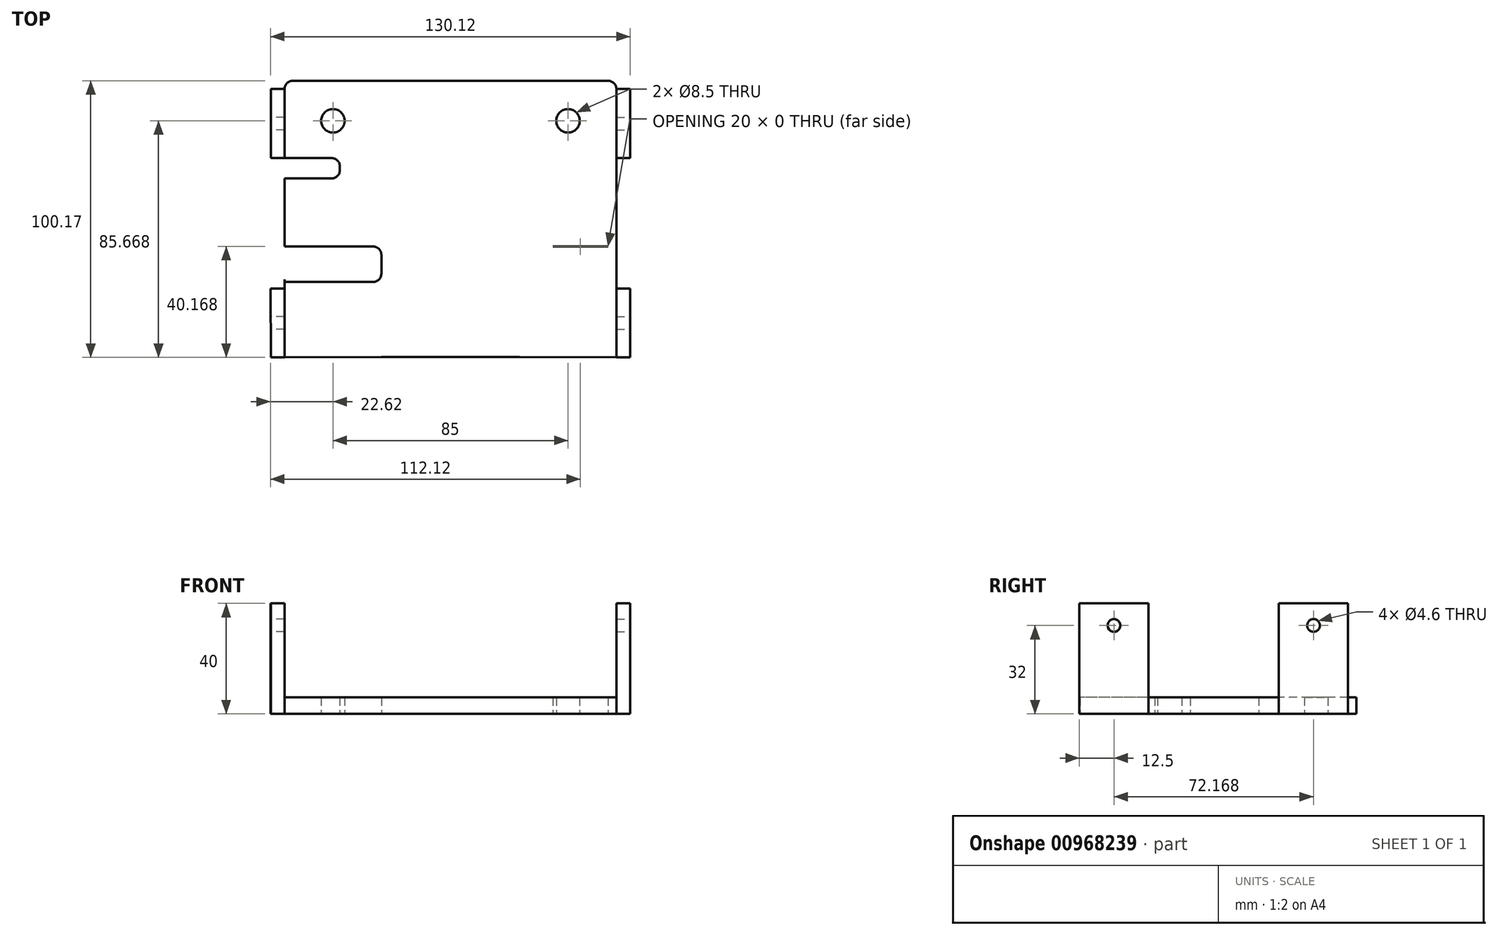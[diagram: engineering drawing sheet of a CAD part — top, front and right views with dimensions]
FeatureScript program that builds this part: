
annotation { "Feature Type Name" : "Feature", "Feature Type Description" : "" }
export const myFeature = defineFeature(function(context is Context, id is Id, definition is map)
    precondition{}
    {
        {
            var Q0;
            Q0=qCreatedBy(makeId("Top.planeOp"),FACE);
            var sketch = newSketch(context, id + "F0", { "sketchPlane" : qUnion([Q0])});
            skLineSegment(sketch, "E0", {"start": v(0, 92.02) * mm, "end": v(0, -91.78) * mm, "construction": true});
            skLineSegment(sketch, "E1", {"start": v(0, -91.78) * mm, "end": v(0, 0) * mm, "construction": true});
            skLineSegment(sketch, "E2", {"start": v(0, 0) * mm, "end": v(-91.17, 0) * mm, "construction": true});
            skLineSegment(sketch, "E3", {"start": v(-91.17, 0) * mm, "end": v(91.17, 0) * mm, "construction": true});
            skLineSegment(sketch, "E4", {"start": v(0, 70.73) * mm, "end": v(-57, 70.73) * mm});
            skLineSegment(sketch, "E5", {"start": v(-57, 10.73) * mm, "end": v(-28, 10.73) * mm});
            skLineSegment(sketch, "E6", {"start": v(-25, -29.27) * mm, "end": v(0, -29.27) * mm});
            skLineSegment(sketch, "E7.MirrorCS", {"start": v(0, 70.73) * mm, "end": v(57, 70.73) * mm});
            skLineSegment(sketch, "E8.MirrorCS", {"start": v(25, -29.27) * mm, "end": v(0, -29.27) * mm});
            skLineSegment(sketch, "E9", {"start": v(37, 10.73) * mm, "end": v(28, 10.73) * mm});
            skCircle(sketch, "E10", {"center": v(42.5, 56.23) * mm, "radius": 4.25 * mm});
            skCircle(sketch, "E11.MirrorC", {"center": v(-42.5, 56.23) * mm, "radius": 4.25 * mm});
            skLineSegment(sketch, "E12", {"start": v(-28, -2.13) * mm, "end": v(-57, -2.13) * mm});
            skLineSegment(sketch, "E13", {"start": v(-60, -29.44) * mm, "end": v(-25, -29.27) * mm});
            skPoint(sketch, "E14.visualSharp", {"position": v(-25, 10.73) * mm});
            skArc(sketch, "E14.filletArc", {"start": v(-25, 7.65) * mm, "mid": v(-25.85, 9.82) * mm, "end": v(-28, 10.73) * mm});
            skLineSegment(sketch, "E15", {"start": v(-25, 0.87) * mm, "end": v(-25, 7.65) * mm});
            skPoint(sketch, "E16.visualSharp", {"position": v(-25, -2.13) * mm});
            skArc(sketch, "E16.filletArc", {"start": v(-28, -2.13) * mm, "mid": v(-25.88, -1.25) * mm, "end": v(-25, 0.87) * mm});
            skLineSegment(sketch, "E17.MirrorCS", {"start": v(60, -29.44) * mm, "end": v(25, -29.27) * mm});
            skLineSegment(sketch, "E18", {"start": v(57, -2.13) * mm, "end": v(28, -2.13) * mm});
            skLineSegment(sketch, "E19", {"start": v(25, 7.73) * mm, "end": v(25, 0.87) * mm});
            skPoint(sketch, "E20.visualSharp", {"position": v(25, 10.73) * mm});
            skArc(sketch, "E20.filletArc", {"start": v(28, 10.73) * mm, "mid": v(25.88, 9.85) * mm, "end": v(25, 7.73) * mm});
            skPoint(sketch, "E21.visualSharp", {"position": v(25, -2.13) * mm});
            skArc(sketch, "E21.filletArc", {"start": v(25, 0.87) * mm, "mid": v(25.88, -1.25) * mm, "end": v(28, -2.13) * mm});
            skPoint(sketch, "E22.visualSharp", {"position": v(40, 42.73) * mm});
            skPoint(sketch, "E23.visualSharp", {"position": v(-60, 70.73) * mm});
            skArc(sketch, "E23.filletArc", {"start": v(-57, 70.73) * mm, "mid": v(-59.12, 69.85) * mm, "end": v(-60, 67.73) * mm});
            skPoint(sketch, "E24.visualSharp", {"position": v(60, 70.73) * mm});
            skArc(sketch, "E24.filletArc", {"start": v(60, 67.73) * mm, "mid": v(59.12, 69.85) * mm, "end": v(57, 70.73) * mm});
            skLineSegment(sketch, "E25.0", {"start": v(65, -4.44) * mm, "end": v(65, -29.44) * mm});
            skLineSegment(sketch, "E26.0", {"start": v(65, 67.73) * mm, "end": v(65, 42.73) * mm});
            skLineSegment(sketch, "E27", {"start": v(65, 67.73) * mm, "end": v(60, 67.73) * mm});
            skLineSegment(sketch, "E28", {"start": v(65, -29.44) * mm, "end": v(60, -29.44) * mm});
            skLineSegment(sketch, "E29", {"start": v(-60, -29.44) * mm, "end": v(-65, -29.44) * mm});
            skLineSegment(sketch, "E30", {"start": v(37, 10.73) * mm, "end": v(57, 10.73) * mm});
            skLineSegment(sketch, "E31", {"start": v(-57, 10.73) * mm, "end": v(-60, 10.73) * mm});
            skLineSegment(sketch, "E32", {"start": v(-60, -2.13) * mm, "end": v(-57, -2.13) * mm});
            skLineSegment(sketch, "E33", {"start": v(-60, 10.73) * mm, "end": v(-60, -2.13) * mm});
            skPoint(sketch, "E34.visualSharp", {"position": v(60, 42.73) * mm});
            skPoint(sketch, "E35.visualSharp", {"position": v(60, 35.38) * mm});
            skLineSegment(sketch, "E36", {"start": v(60, 0.87) * mm, "end": v(60, 7.73) * mm});
            skLineSegment(sketch, "E37", {"start": v(57, 10.73) * mm, "end": v(28, 10.73) * mm});
            skPoint(sketch, "E38.visualSharp", {"position": v(60, 10.73) * mm});
            skPoint(sketch, "E39.visualSharp", {"position": v(60, -2.13) * mm});
            skLineSegment(sketch, "E40", {"start": v(-60, 67.73) * mm, "end": v(-60, -29.44) * mm});
            skLineSegment(sketch, "E41", {"start": v(60, 67.73) * mm, "end": v(60, -29.44) * mm});
            skLineSegment(sketch, "E42", {"start": v(-60, 10.73) * mm, "end": v(-28, 10.73) * mm});
            skLineSegment(sketch, "E43", {"start": v(-28, -2.13) * mm, "end": v(-60, -2.13) * mm});
            skLineSegment(sketch, "E44", {"start": v(-60, 67.73) * mm, "end": v(-65, 67.73) * mm});
            skLineSegment(sketch, "E45", {"start": v(-65, 67.73) * mm, "end": v(-65, 42.73) * mm});
            skLineSegment(sketch, "E46", {"start": v(-65, 42.73) * mm, "end": v(-60, 42.73) * mm});
            skLineSegment(sketch, "E47", {"start": v(-65, -29.44) * mm, "end": v(-65.12, -4.44) * mm});
            skLineSegment(sketch, "E48", {"start": v(-65.12, -4.44) * mm, "end": v(-60, -4.44) * mm});
            skLineSegment(sketch, "E49", {"start": v(65, 42.73) * mm, "end": v(60, 42.73) * mm});
            skLineSegment(sketch, "E50", {"start": v(65, -4.44) * mm, "end": v(60, -4.44) * mm});
            skLineSegment(sketch, "E51", {"start": v(-65, -29.44) * mm, "end": v(65, -29.44) * mm});
            skLineSegment(sketch, "E52", {"start": v(-65, 42.73) * mm, "end": v(65, 42.73) * mm});
            skLineSegment(sketch, "E53.MirrorCS", {"start": v(-57, 35.38) * mm, "end": v(-43, 35.38) * mm});
            skArc(sketch, "E54.MirrorCS", {"start": v(-40, 38.38) * mm, "mid": v(-40.88, 36.26) * mm, "end": v(-43, 35.38) * mm});
            skArc(sketch, "E55.MirrorCS", {"start": v(-43, 42.73) * mm, "mid": v(-40.88, 41.85) * mm, "end": v(-40, 39.73) * mm});
            skLineSegment(sketch, "E56.MirrorCS", {"start": v(-40, 39.73) * mm, "end": v(-40, 38.38) * mm});
            skLineSegment(sketch, "E57.MirrorCS", {"start": v(-43, 42.73) * mm, "end": v(-57, 42.73) * mm});
            skLineSegment(sketch, "E58.MirrorCS", {"start": v(-60, 39.73) * mm, "end": v(-60, 38.38) * mm});
            skLineSegment(sketch, "E59", {"start": v(37, 10.73) * mm, "end": v(60, 10.73) * mm});
            skLineSegment(sketch, "E60", {"start": v(57, -2.13) * mm, "end": v(60, -2.13) * mm});
            skLineSegment(sketch, "E61", {"start": v(-57, 42.73) * mm, "end": v(-60, 42.73) * mm});
            skLineSegment(sketch, "E62", {"start": v(-57, 35.38) * mm, "end": v(-60, 35.38) * mm});
            skLineSegment(sketch, "E63", {"start": v(-60, 35.38) * mm, "end": v(-60, 42.73) * mm});
            skSolve(sketch);
        }
        {
            var Q0;
            Q0=makeQuery(id+"F0.imprint","IMPRINT",FACE,{"disambiguationData":[TD([[makeQuery(id+"F0.imprint","IMPRINT",EDGE,{"derivedFrom":sQuery(id+"F0.wireOp",EDGE,"d9c65f52-a5ec-4b5d-bf31-9a5a10682f11.0")}),1.0]])]});
            var Q1;
            Q1=makeQuery(id+"F0.imprint","IMPRINT",FACE,{"disambiguationData":[TD([[makeQuery(id+"F0.imprint","IMPRINT",EDGE,{"derivedFrom":sQuery(id+"F0.wireOp",EDGE,"E25.0")}),-1.0]])]});
            var Q2;
            Q2=makeQuery(id+"F0.imprint","IMPRINT",FACE,{"disambiguationData":[TD([[makeQuery(id+"F0.imprint","IMPRINT",EDGE,{"derivedFrom":sQuery(id+"F0.wireOp",EDGE,"E26.0")}),-1.0]])]});
            var Q3;
            {var subQ0=sQuery(id+"F0.wireOp",EDGE,"E44");Q3=makeQuery(id+"F0.imprint","IMPRINT",FACE,{"disambiguationData":[TD([[makeQuery(id+"F0.imprint","IMPRINT",EDGE,{"derivedFrom":subQ0}),1.0]])]});}
            var Q4;
            {var subQ0=sQuery(id+"F0.wireOp",EDGE,"E29");Q4=makeQuery(id+"F0.imprint","IMPRINT",FACE,{"disambiguationData":[TD([[makeQuery(id+"F0.imprint","IMPRINT",EDGE,{"derivedFrom":subQ0}),-1.0]])]});}
            var Q5;
            {var subQ4=sQuery(id+"F0.wireOp",EDGE,"E47");Q5=makeQuery(id+"F0.imprint","IMPRINT",FACE,{"disambiguationData":[TD([[makeQuery(id+"F0.imprint","IMPRINT",EDGE,{"derivedFrom":subQ4}),-1.0]])]});}
            extrude(context, id + "F1", {"entities" : qUnion([Q0, Q1, Q2, Q3, Q4, Q5]), "depth" : 40 * mm, "offsetDistance" : 25 * mm});
        }
        {
            var Q0;
            Q0=makeQuery(id+"F0.imprint","IMPRINT",FACE,{"disambiguationData":[TD([[makeQuery(id+"F0.imprint","IMPRINT",EDGE,{"derivedFrom":sQuery(id+"F0.wireOp",EDGE,"E4")}),1.0]])]});
            var Q1;
            Q1=makeQuery(id+"F0.imprint","IMPRINT",FACE,{"disambiguationData":[TD([[makeQuery(id+"F0.imprint","IMPRINT",EDGE,{"derivedFrom":sQuery(id+"F0.wireOp",EDGE,"E6")}),1.0]])]});
            extrude(context, id + "F2", {"entities" : qUnion([Q0, Q1]), "depth" : 6 * mm, "offsetDistance" : 25 * mm});
        }
        {
            var Q0;
            Q0=makeQuery(id+"F1.opExtrude","SWEPT_FACE",FACE,{"disambiguationData":[OSD([sQuery(id+"F0.wireOp",EDGE,"E45")])]});
            var sketch = newSketch(context, id + "F3", { "sketchPlane" : qUnion([Q0])});
            skCircle(sketch, "E64", {"center": v(-55.23, 32) * mm, "radius": 2.3 * mm});
            skSolve(sketch);
        }
        {
            var Q0;
            Q0 = qSketchRegion(id + "F3", true);
            extrude(context, id + "F4", {"entities" : qUnion([Q0]), "operationType" : NewBodyOperationType.REMOVE, "oppositeDirection" : true, "depth" : 5 * mm, "offsetDistance" : 25 * mm});
        }
        {
            var Q0;
            Q0=makeQuery(id+"F1.opExtrude","SWEPT_FACE",FACE,{"disambiguationData":[OSD([sQuery(id+"F0.wireOp",EDGE,"E47")])]});
            var sketch = newSketch(context, id + "F5", { "sketchPlane" : qUnion([Q0])});
            skCircle(sketch, "E65", {"center": v(16.63, 32) * mm, "radius": 2.3 * mm});
            skSolve(sketch);
        }
        {
            var Q0;
            Q0 = qSketchRegion(id + "F5", true);
            extrude(context, id + "F6", {"entities" : qUnion([Q0]), "operationType" : NewBodyOperationType.REMOVE, "oppositeDirection" : true, "depth" : 6 * mm, "offsetDistance" : 25 * mm});
        }
        {
            var Q0;
            Q0=makeQuery(id+"F1.opExtrude","SWEPT_FACE",FACE,{"disambiguationData":[OSD([sQuery(id+"F0.wireOp",EDGE,"E25.0")])]});
            var sketch = newSketch(context, id + "F7", { "sketchPlane" : qUnion([Q0])});
            skCircle(sketch, "E66", {"center": v(-16.94, 32) * mm, "radius": 2.3 * mm});
            skSolve(sketch);
        }
        {
            var Q0;
            Q0=makeQuery(id+"F7.imprint","IMPRINT",FACE,{"disambiguationData":[TD([[makeQuery(id+"F7.imprint","IMPRINT",EDGE,{"derivedFrom":sQuery(id+"F7.wireOp",EDGE,"E66")}),1.0]])]});
            extrude(context, id + "F8", {"entities" : qUnion([Q0]), "operationType" : NewBodyOperationType.REMOVE, "oppositeDirection" : true, "depth" : 6 * mm, "offsetDistance" : 25 * mm});
        }
        {
            var Q0;
            Q0=makeQuery(id+"F1.opExtrude","SWEPT_FACE",FACE,{"disambiguationData":[OSD([sQuery(id+"F0.wireOp",EDGE,"E26.0")])]});
            var sketch = newSketch(context, id + "F9", { "sketchPlane" : qUnion([Q0])});
            skCircle(sketch, "E67", {"center": v(55.23, 32) * mm, "radius": 2.3 * mm});
            skSolve(sketch);
        }
        {
            var Q0;
            Q0=makeQuery(id+"F9.imprint","IMPRINT",FACE,{"disambiguationData":[TD([[makeQuery(id+"F9.imprint","IMPRINT",EDGE,{"derivedFrom":sQuery(id+"F9.wireOp",EDGE,"E67")}),1.0]])]});
            extrude(context, id + "F10", {"entities" : qUnion([Q0]), "operationType" : NewBodyOperationType.REMOVE, "oppositeDirection" : true, "depth" : 6 * mm, "offsetDistance" : 25 * mm});
        }
    });
